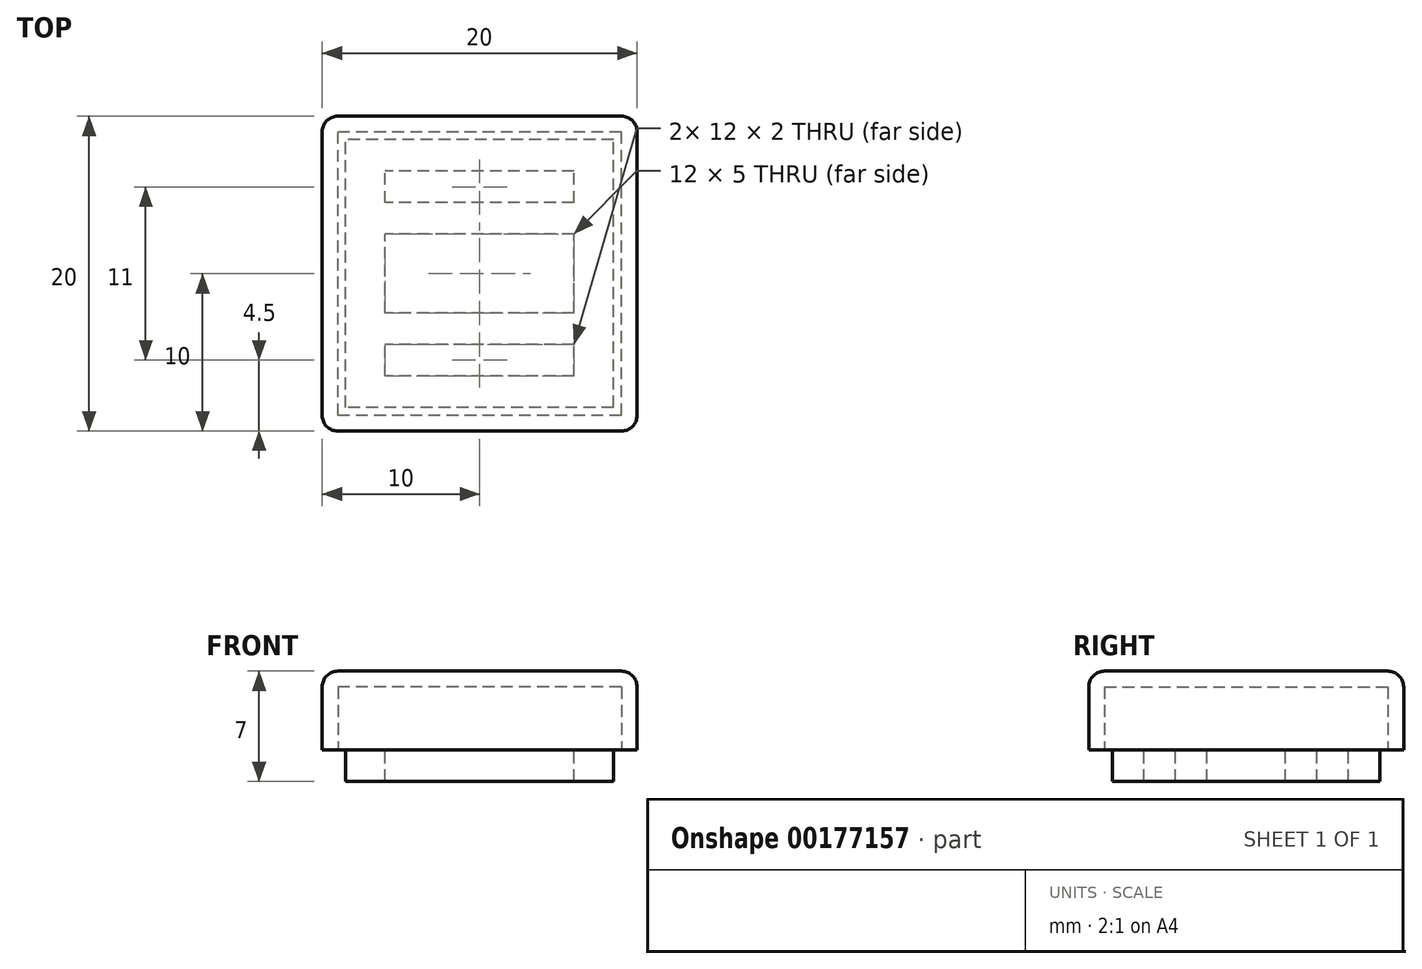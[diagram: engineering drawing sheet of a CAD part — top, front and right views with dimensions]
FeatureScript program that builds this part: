
annotation { "Feature Type Name" : "Feature", "Feature Type Description" : "" }
export const myFeature = defineFeature(function(context is Context, id is Id, definition is map)
    precondition{}
    {
        {
            var Q0;
            Q0=qCreatedBy(makeId("Top.planeOp"),FACE);
            var sketch = newSketch(context, id + "F0", { "sketchPlane" : qUnion([Q0])});
            skLineSegment(sketch, "E0.bottom", {"start": v(10, -10) * mm, "end": v(-10, -10) * mm});
            skLineSegment(sketch, "E0.top", {"start": v(10, 10) * mm, "end": v(-10, 10) * mm});
            skLineSegment(sketch, "E0.left", {"start": v(10, -10) * mm, "end": v(10, 10) * mm});
            skLineSegment(sketch, "E0.right", {"start": v(-10, -10) * mm, "end": v(-10, 10) * mm});
            skPoint(sketch, "E0.middle", {"position": v(0, 0) * mm});
            skSolve(sketch);
        }
        {
            var Q0;
            Q0 = qSketchRegion(id + "F0", true);
            extrude(context, id + "F1", {"entities" : qUnion([Q0]), "depth" : 5 * mm});
        }
        {
            var Q0;
            Q0=makeQuery(id+"F1.opExtrude","CAP_FACE",FACE,{"disambiguationData":[OSD([sQuery(id+"F0.wireOp",EDGE,"E0.bottom"),sQuery(id+"F0.wireOp",EDGE,"E0.top"),sQuery(id+"F0.wireOp",EDGE,"E0.left"),sQuery(id+"F0.wireOp",EDGE,"E0.right")])],"isStart":true});
            shell(context, id + "F2", {"entities" : qUnion([Q0]), "thickness" : 1 * mm});
        }
        {
            var Q0;
            Q0=makeQuery(id+"F1.opExtrude","CAP_FACE",FACE,{"disambiguationData":[OSD([sQuery(id+"F0.wireOp",EDGE,"E0.bottom"),sQuery(id+"F0.wireOp",EDGE,"E0.top"),sQuery(id+"F0.wireOp",EDGE,"E0.left"),sQuery(id+"F0.wireOp",EDGE,"E0.right")])],"isStart":false});
            var Q1;
            Q1=makeQuery(id+"F1.opExtrude","SWEPT_EDGE",EDGE,{"disambiguationData":[OSD([sQuery(id+"F0.wireOp",EDGE,"E0.bottom"),sQuery(id+"F0.wireOp",EDGE,"E0.right")])]});
            var Q2;
            Q2=makeQuery(id+"F1.opExtrude","SWEPT_EDGE",EDGE,{"disambiguationData":[OSD([sQuery(id+"F0.wireOp",EDGE,"E0.bottom"),sQuery(id+"F0.wireOp",EDGE,"E0.left")])]});
            var Q3;
            Q3=makeQuery(id+"F1.opExtrude","SWEPT_EDGE",EDGE,{"disambiguationData":[OSD([sQuery(id+"F0.wireOp",EDGE,"E0.top"),sQuery(id+"F0.wireOp",EDGE,"E0.left")])]});
            var Q4;
            Q4=makeQuery(id+"F1.opExtrude","SWEPT_EDGE",EDGE,{"disambiguationData":[OSD([sQuery(id+"F0.wireOp",EDGE,"E0.top"),sQuery(id+"F0.wireOp",EDGE,"E0.right")])]});
            fillet(context, id + "F3", {"entities" : qUnion([Q0, Q1, Q2, Q3, Q4]), "radius" : 1 * mm, "tangentPropagation" : true, "allowEdgeOverflow" : false});
        }
        {
            var Q0;
            Q0=qCreatedBy(makeId("Top.planeOp"),FACE);
            var sketch = newSketch(context, id + "F4", { "sketchPlane" : qUnion([Q0])});
            skLineSegment(sketch, "E1.bottom", {"start": v(8.5, -8.5) * mm, "end": v(-8.5, -8.5) * mm});
            skLineSegment(sketch, "E1.top", {"start": v(8.5, 8.5) * mm, "end": v(-8.5, 8.5) * mm});
            skLineSegment(sketch, "E1.left", {"start": v(8.5, -8.5) * mm, "end": v(8.5, 8.5) * mm});
            skLineSegment(sketch, "E1.right", {"start": v(-8.5, -8.5) * mm, "end": v(-8.5, 8.5) * mm});
            skPoint(sketch, "E1.middle", {"position": v(0, 0) * mm});
            skLineSegment(sketch, "E2.bottom", {"start": v(6, -2.5) * mm, "end": v(-6, -2.5) * mm});
            skLineSegment(sketch, "E2.top", {"start": v(6, 2.5) * mm, "end": v(-6, 2.5) * mm});
            skLineSegment(sketch, "E2.left", {"start": v(6, -2.5) * mm, "end": v(6, 2.5) * mm});
            skLineSegment(sketch, "E2.right", {"start": v(-6, -2.5) * mm, "end": v(-6, 2.5) * mm});
            skLineSegment(sketch, "E3.bottom", {"start": v(6, 4.5) * mm, "end": v(-6, 4.5) * mm});
            skLineSegment(sketch, "E3.top", {"start": v(6, 6.5) * mm, "end": v(-6, 6.5) * mm});
            skLineSegment(sketch, "E3.left", {"start": v(6, 4.5) * mm, "end": v(6, 6.5) * mm});
            skLineSegment(sketch, "E3.right", {"start": v(-6, 4.5) * mm, "end": v(-6, 6.5) * mm});
            skPoint(sketch, "E3.middle", {"position": v(0, 5.5) * mm});
            skLineSegment(sketch, "E4.bottom", {"start": v(6, -6.5) * mm, "end": v(-6, -6.5) * mm});
            skLineSegment(sketch, "E4.top", {"start": v(6, -4.5) * mm, "end": v(-6, -4.5) * mm});
            skLineSegment(sketch, "E4.left", {"start": v(6, -6.5) * mm, "end": v(6, -4.5) * mm});
            skLineSegment(sketch, "E4.right", {"start": v(-6, -6.5) * mm, "end": v(-6, -4.5) * mm});
            skPoint(sketch, "E4.middle", {"position": v(0, -5.5) * mm});
            skLineSegment(sketch, "E5", {"start": v(-6.23, 3.5) * mm, "end": v(6.3, 3.5) * mm, "construction": true});
            skLineSegment(sketch, "E6", {"start": v(-6.74, -3.5) * mm, "end": v(5.67, -3.5) * mm, "construction": true});
            skSolve(sketch);
        }
        {
            var Q0;
            Q0 = qSketchRegion(id + "F4", true);
            extrude(context, id + "F5", {"entities" : qUnion([Q0]), "oppositeDirection" : true, "depth" : 2 * mm});
        }
    });
